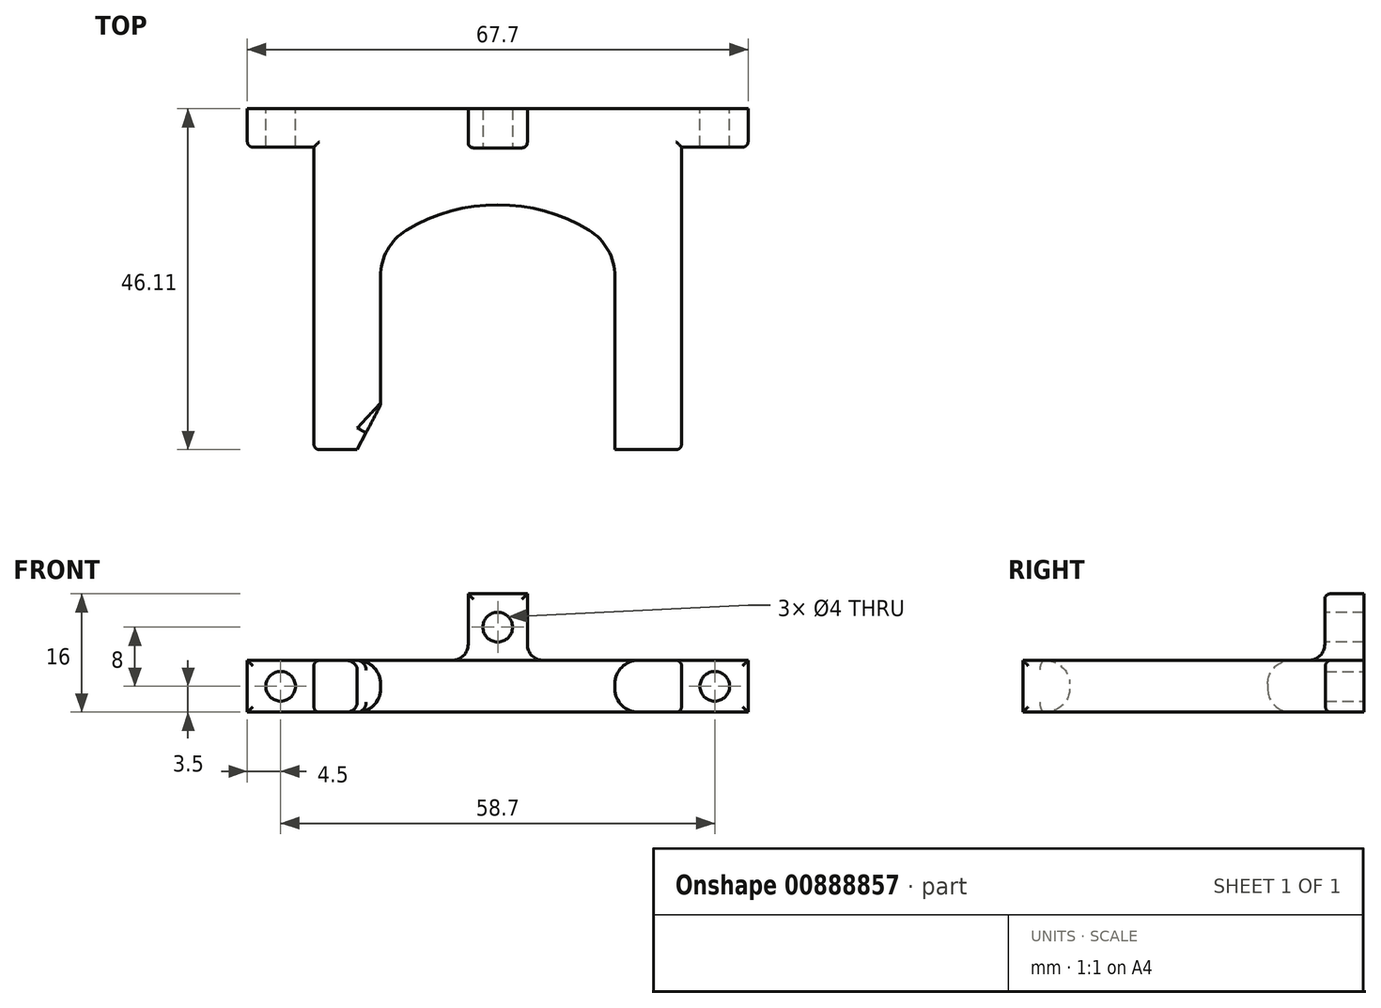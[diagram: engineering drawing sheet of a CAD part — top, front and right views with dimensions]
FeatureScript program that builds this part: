
annotation { "Feature Type Name" : "Feature", "Feature Type Description" : "" }
export const myFeature = defineFeature(function(context is Context, id is Id, definition is map)
    precondition{}
    {
        {
            var Q0;
            Q0=qCreatedBy(makeId("Top.planeOp"),FACE);
            var sketch = newSketch(context, id + "F0", { "sketchPlane" : qUnion([Q0])});
            skLineSegment(sketch, "E0", {"start": v(-15.85, 0) * mm, "end": v(-15.85, -27.08) * mm});
            skLineSegment(sketch, "E1", {"start": v(-15.85, -27.08) * mm, "end": v(-24.85, -27.08) * mm});
            skLineSegment(sketch, "E2", {"start": v(-24.85, -27.08) * mm, "end": v(-24.85, 19.03) * mm});
            skLineSegment(sketch, "E3", {"start": v(-24.85, 19.03) * mm, "end": v(24.85, 19.03) * mm});
            skLineSegment(sketch, "E4", {"start": v(24.85, 19.03) * mm, "end": v(24.85, -27.08) * mm});
            skLineSegment(sketch, "E5", {"start": v(24.85, -27.08) * mm, "end": v(15.85, -27.08) * mm});
            skLineSegment(sketch, "E6", {"start": v(15.85, -27.08) * mm, "end": v(15.85, 0) * mm});
            skPoint(sketch, "E7", {"position": v(0, 0) * mm});
            skPoint(sketch, "E8", {"position": v(0, 19.03) * mm});
            skArc(sketch, "E9", {"start": v(15.85, 0) * mm, "mid": v(0, 6.03) * mm, "end": v(-15.85, 0) * mm});
            skSolve(sketch);
        }
        {
            var Q0;
            Q0 = qSketchRegion(id + "F0", true);
            extrude(context, id + "F1", {"entities" : qUnion([Q0]), "depth" : 7 * mm, "offsetDistance" : 25 * mm});
        }
        {
            var Q0;
            Q0=makeQuery(id+"F1.opExtrude","SWEPT_EDGE",EDGE,{"disambiguationData":[OSD([sQuery(id+"F0.wireOp",EDGE,"E0"),sQuery(id+"F0.wireOp",EDGE,"E9")])]});
            var Q1;
            Q1=makeQuery(id+"F1.opExtrude","SWEPT_EDGE",EDGE,{"disambiguationData":[OSD([sQuery(id+"F0.wireOp",EDGE,"E6"),sQuery(id+"F0.wireOp",EDGE,"E9")])]});
            fillet(context, id + "F2", {"entities" : qUnion([Q0, Q1]), "radius" : 7.3 * mm, "tangentPropagation" : true, "allowEdgeOverflow" : false});
        }
        {
            var Q0;
            Q0=makeQuery(id+"F1.opExtrude","CAP_EDGE",EDGE,{"disambiguationData":[OSD([sQuery(id+"F0.wireOp",EDGE,"E0")])],"isStart":false});
            var Q1;
            {var subQ0=sQuery(id+"F0.wireOp",EDGE,"E9");var subQ1=sQuery(id+"F0.wireOp",EDGE,"E0");Q1=makeQuery(id+"F2.opFillet","BLEND_EDGE",EDGE,{"blendedFrom":[makeQuery(id+"F1.opExtrude","SWEPT_EDGE",EDGE,{"disambiguationData":[OSD([subQ1,subQ0])]}),makeQuery(id+"F1.opExtrude","CAP_FACE",FACE,{"disambiguationData":[OSD([subQ1,sQuery(id+"F0.wireOp",EDGE,"E1"),sQuery(id+"F0.wireOp",EDGE,"E2"),sQuery(id+"F0.wireOp",EDGE,"E3"),sQuery(id+"F0.wireOp",EDGE,"E4"),sQuery(id+"F0.wireOp",EDGE,"E5"),sQuery(id+"F0.wireOp",EDGE,"E6"),subQ0])],"isStart":false})],"blendedInto":[makeQuery(id+"F1.opExtrude","CAP_FACE",FACE,{"disambiguationData":[OSD([subQ1,sQuery(id+"F0.wireOp",EDGE,"E1"),sQuery(id+"F0.wireOp",EDGE,"E2"),sQuery(id+"F0.wireOp",EDGE,"E3"),sQuery(id+"F0.wireOp",EDGE,"E4"),sQuery(id+"F0.wireOp",EDGE,"E5"),sQuery(id+"F0.wireOp",EDGE,"E6"),subQ0])],"isStart":false})]});}
            var Q2;
            Q2=makeQuery(id+"F1.opExtrude","CAP_EDGE",EDGE,{"disambiguationData":[OSD([sQuery(id+"F0.wireOp",EDGE,"E9")])],"isStart":false});
            var Q3;
            {var subQ0=sQuery(id+"F0.wireOp",EDGE,"E9");var subQ1=sQuery(id+"F0.wireOp",EDGE,"E6");Q3=makeQuery(id+"F2.opFillet","BLEND_EDGE",EDGE,{"blendedFrom":[makeQuery(id+"F1.opExtrude","SWEPT_EDGE",EDGE,{"disambiguationData":[OSD([subQ1,subQ0])]}),makeQuery(id+"F1.opExtrude","CAP_FACE",FACE,{"disambiguationData":[OSD([sQuery(id+"F0.wireOp",EDGE,"E0"),sQuery(id+"F0.wireOp",EDGE,"E1"),sQuery(id+"F0.wireOp",EDGE,"E2"),sQuery(id+"F0.wireOp",EDGE,"E3"),sQuery(id+"F0.wireOp",EDGE,"E4"),sQuery(id+"F0.wireOp",EDGE,"E5"),subQ1,subQ0])],"isStart":false})],"blendedInto":[makeQuery(id+"F1.opExtrude","CAP_FACE",FACE,{"disambiguationData":[OSD([sQuery(id+"F0.wireOp",EDGE,"E0"),sQuery(id+"F0.wireOp",EDGE,"E1"),sQuery(id+"F0.wireOp",EDGE,"E2"),sQuery(id+"F0.wireOp",EDGE,"E3"),sQuery(id+"F0.wireOp",EDGE,"E4"),sQuery(id+"F0.wireOp",EDGE,"E5"),subQ1,subQ0])],"isStart":false})]});}
            var Q4;
            Q4=makeQuery(id+"F1.opExtrude","CAP_EDGE",EDGE,{"disambiguationData":[OSD([sQuery(id+"F0.wireOp",EDGE,"E6")])],"isStart":false});
            var Q5;
            Q5=makeQuery(id+"F1.opExtrude","CAP_EDGE",EDGE,{"disambiguationData":[OSD([sQuery(id+"F0.wireOp",EDGE,"E6")])],"isStart":true});
            var Q6;
            {var subQ0=sQuery(id+"F0.wireOp",EDGE,"E9");var subQ1=sQuery(id+"F0.wireOp",EDGE,"E6");Q6=makeQuery(id+"F2.opFillet","BLEND_EDGE",EDGE,{"blendedFrom":[makeQuery(id+"F1.opExtrude","SWEPT_EDGE",EDGE,{"disambiguationData":[OSD([subQ1,subQ0])]}),makeQuery(id+"F1.opExtrude","CAP_FACE",FACE,{"disambiguationData":[OSD([sQuery(id+"F0.wireOp",EDGE,"E0"),sQuery(id+"F0.wireOp",EDGE,"E1"),sQuery(id+"F0.wireOp",EDGE,"E2"),sQuery(id+"F0.wireOp",EDGE,"E3"),sQuery(id+"F0.wireOp",EDGE,"E4"),sQuery(id+"F0.wireOp",EDGE,"E5"),subQ1,subQ0])],"isStart":true})],"blendedInto":[makeQuery(id+"F1.opExtrude","CAP_FACE",FACE,{"disambiguationData":[OSD([sQuery(id+"F0.wireOp",EDGE,"E0"),sQuery(id+"F0.wireOp",EDGE,"E1"),sQuery(id+"F0.wireOp",EDGE,"E2"),sQuery(id+"F0.wireOp",EDGE,"E3"),sQuery(id+"F0.wireOp",EDGE,"E4"),sQuery(id+"F0.wireOp",EDGE,"E5"),subQ1,subQ0])],"isStart":true})]});}
            var Q7;
            Q7=makeQuery(id+"F1.opExtrude","CAP_EDGE",EDGE,{"disambiguationData":[OSD([sQuery(id+"F0.wireOp",EDGE,"E9")])],"isStart":true});
            var Q8;
            {var subQ0=sQuery(id+"F0.wireOp",EDGE,"E9");var subQ1=sQuery(id+"F0.wireOp",EDGE,"E0");Q8=makeQuery(id+"F2.opFillet","BLEND_EDGE",EDGE,{"blendedFrom":[makeQuery(id+"F1.opExtrude","SWEPT_EDGE",EDGE,{"disambiguationData":[OSD([subQ1,subQ0])]}),makeQuery(id+"F1.opExtrude","CAP_FACE",FACE,{"disambiguationData":[OSD([subQ1,sQuery(id+"F0.wireOp",EDGE,"E1"),sQuery(id+"F0.wireOp",EDGE,"E2"),sQuery(id+"F0.wireOp",EDGE,"E3"),sQuery(id+"F0.wireOp",EDGE,"E4"),sQuery(id+"F0.wireOp",EDGE,"E5"),sQuery(id+"F0.wireOp",EDGE,"E6"),subQ0])],"isStart":true})],"blendedInto":[makeQuery(id+"F1.opExtrude","CAP_FACE",FACE,{"disambiguationData":[OSD([subQ1,sQuery(id+"F0.wireOp",EDGE,"E1"),sQuery(id+"F0.wireOp",EDGE,"E2"),sQuery(id+"F0.wireOp",EDGE,"E3"),sQuery(id+"F0.wireOp",EDGE,"E4"),sQuery(id+"F0.wireOp",EDGE,"E5"),sQuery(id+"F0.wireOp",EDGE,"E6"),subQ0])],"isStart":true})]});}
            var Q9;
            Q9=makeQuery(id+"F1.opExtrude","CAP_EDGE",EDGE,{"disambiguationData":[OSD([sQuery(id+"F0.wireOp",EDGE,"E0")])],"isStart":true});
            fillet(context, id + "F3", {"entities" : qUnion([Q0, Q1, Q2, Q3, Q4, Q5, Q6, Q7, Q8, Q9]), "radius" : 3.14 * mm, "tangentPropagation" : true, "allowEdgeOverflow" : false});
        }
        {
            var Q0;
            Q0=makeQuery(id+"F1.opExtrude","SWEPT_FACE",FACE,{"disambiguationData":[OSD([sQuery(id+"F0.wireOp",EDGE,"E3")])]});
            var sketch = newSketch(context, id + "F4", { "sketchPlane" : qUnion([Q0])});
            skPoint(sketch, "E10", {"position": v(0, 7) * mm});
            skLineSegment(sketch, "E11.bottom", {"start": v(-4, 7) * mm, "end": v(4, 7) * mm});
            skLineSegment(sketch, "E11.top", {"start": v(-4, 16) * mm, "end": v(4, 16) * mm});
            skLineSegment(sketch, "E11.left", {"start": v(-4, 7) * mm, "end": v(-4, 16) * mm});
            skLineSegment(sketch, "E11.right", {"start": v(4, 7) * mm, "end": v(4, 16) * mm});
            skPoint(sketch, "E12", {"position": v(0, 16) * mm});
            skSolve(sketch);
        }
        {
            var Q0;
            Q0 = qSketchRegion(id + "F4", true);
            extrude(context, id + "F5", {"entities" : qUnion([Q0]), "operationType" : NewBodyOperationType.ADD, "oppositeDirection" : true, "depth" : 5.3 * mm, "offsetDistance" : 25 * mm});
        }
        {
            var Q0;
            Q0=makeQuery(id+"F5.opExtrude","CAP_FACE",FACE,{"disambiguationData":[OSD([sQuery(id+"F4.wireOp",EDGE,"E11.bottom"),sQuery(id+"F4.wireOp",EDGE,"E11.top"),sQuery(id+"F4.wireOp",EDGE,"E11.left"),sQuery(id+"F4.wireOp",EDGE,"E11.right")])],"isStart":false});
            var sketch = newSketch(context, id + "F6", { "sketchPlane" : qUnion([Q0])});
            skPoint(sketch, "E13", {"position": v(0, 11.5) * mm});
            skCircle(sketch, "E14", {"center": v(0, 11.5) * mm, "radius": 2 * mm});
            skSolve(sketch);
        }
        {
            var Q0;
            Q0 = qSketchRegion(id + "F6", true);
            extrude(context, id + "F7", {"entities" : qUnion([Q0]), "operationType" : NewBodyOperationType.REMOVE, "oppositeDirection" : true, "depth" : 25 * mm, "offsetDistance" : 25 * mm});
        }
        {
            var Q0;
            Q0=makeQuery(id+"F5.boolean.opBoolean","MERGE",FACE,{"derivedFrom":[makeQuery(id+"F1.opExtrude","SWEPT_FACE",FACE,{"disambiguationData":[OSD([sQuery(id+"F0.wireOp",EDGE,"E3")])]}),makeQuery(id+"F5.opExtrude","CAP_FACE",FACE,{"disambiguationData":[OSD([sQuery(id+"F4.wireOp",EDGE,"E11.bottom"),sQuery(id+"F4.wireOp",EDGE,"E11.top"),sQuery(id+"F4.wireOp",EDGE,"E11.left"),sQuery(id+"F4.wireOp",EDGE,"E11.right")])],"isStart":true})]});
            var sketch = newSketch(context, id + "F8", { "sketchPlane" : qUnion([Q0])});
            skLineSegment(sketch, "E15.bottom", {"start": v(24.85, 7) * mm, "end": v(33.85, 7) * mm});
            skLineSegment(sketch, "E15.top", {"start": v(24.85, 0) * mm, "end": v(33.85, 0) * mm});
            skLineSegment(sketch, "E15.left", {"start": v(24.85, 7) * mm, "end": v(24.85, 0) * mm});
            skLineSegment(sketch, "E15.right", {"start": v(33.85, 7) * mm, "end": v(33.85, 0) * mm});
            skLineSegment(sketch, "E16", {"start": v(0, 32.28) * mm, "end": v(0, -10.36) * mm});
            skPoint(sketch, "E16.endSnap0", {"position": v(0, 16) * mm});
            skLineSegment(sketch, "E17.MirrorCS", {"start": v(-24.85, 7) * mm, "end": v(-24.85, 0) * mm});
            skLineSegment(sketch, "E18.MirrorCS", {"start": v(-33.85, 7) * mm, "end": v(-33.85, 0) * mm});
            skLineSegment(sketch, "E19.MirrorCS", {"start": v(-24.85, 7) * mm, "end": v(-33.85, 7) * mm});
            skLineSegment(sketch, "E20.MirrorCS", {"start": v(-24.85, 0) * mm, "end": v(-33.85, 0) * mm});
            skSolve(sketch);
        }
        {
            var Q0;
            Q0 = qSketchRegion(id + "F8", true);
            extrude(context, id + "F9", {"entities" : qUnion([Q0]), "oppositeDirection" : true, "depth" : 5.2 * mm, "offsetDistance" : 25 * mm});
        }
        {
            var Q0;
            Q0=makeQuery(id+"F1.opExtrude","SWEPT_BODY",BODY,{"disambiguationData":[OSD([sQuery(id+"F0.wireOp",EDGE,"E0"),sQuery(id+"F0.wireOp",EDGE,"E1"),sQuery(id+"F0.wireOp",EDGE,"E2"),sQuery(id+"F0.wireOp",EDGE,"E3"),sQuery(id+"F0.wireOp",EDGE,"E4"),sQuery(id+"F0.wireOp",EDGE,"E5"),sQuery(id+"F0.wireOp",EDGE,"E6"),sQuery(id+"F0.wireOp",EDGE,"E9")])]});
            var Q1;
            Q1=makeQuery(id+"F9.opExtrude","SWEPT_BODY",BODY,{"disambiguationData":[OSD([sQuery(id+"F8.wireOp",EDGE,"E15.bottom"),sQuery(id+"F8.wireOp",EDGE,"E15.top"),sQuery(id+"F8.wireOp",EDGE,"E15.left"),sQuery(id+"F8.wireOp",EDGE,"E15.right")])]});
            var Q2;
            Q2=makeQuery(id+"F9.opExtrude","SWEPT_BODY",BODY,{"disambiguationData":[OSD([sQuery(id+"F8.wireOp",EDGE,"E17.MirrorCS"),sQuery(id+"F8.wireOp",EDGE,"E18.MirrorCS"),sQuery(id+"F8.wireOp",EDGE,"E19.MirrorCS"),sQuery(id+"F8.wireOp",EDGE,"E20.MirrorCS")])]});
            booleanBodies(context, id + "F10", {"operationType" : BooleanOperationType.UNION, "tools" : qUnion([Q0, Q1, Q2])});
        }
        {
            var Q0;
            Q0=makeQuery(id+"F10.opBoolean","MERGE",FACE,{"derivedFrom":[makeQuery(id+"F5.boolean.opBoolean","MERGE",FACE,{"derivedFrom":[makeQuery(id+"F1.opExtrude","SWEPT_FACE",FACE,{"disambiguationData":[OSD([sQuery(id+"F0.wireOp",EDGE,"E3")])]}),makeQuery(id+"F5.opExtrude","CAP_FACE",FACE,{"disambiguationData":[OSD([sQuery(id+"F4.wireOp",EDGE,"E11.bottom"),sQuery(id+"F4.wireOp",EDGE,"E11.top"),sQuery(id+"F4.wireOp",EDGE,"E11.left"),sQuery(id+"F4.wireOp",EDGE,"E11.right")])],"isStart":true})]}),makeQuery(id+"F9.opExtrude","CAP_FACE",FACE,{"disambiguationData":[OSD([sQuery(id+"F8.wireOp",EDGE,"E15.bottom"),sQuery(id+"F8.wireOp",EDGE,"E15.top"),sQuery(id+"F8.wireOp",EDGE,"E15.left"),sQuery(id+"F8.wireOp",EDGE,"E15.right")])],"isStart":true}),makeQuery(id+"F9.opExtrude","CAP_FACE",FACE,{"disambiguationData":[OSD([sQuery(id+"F8.wireOp",EDGE,"E17.MirrorCS"),sQuery(id+"F8.wireOp",EDGE,"E18.MirrorCS"),sQuery(id+"F8.wireOp",EDGE,"E19.MirrorCS"),sQuery(id+"F8.wireOp",EDGE,"E20.MirrorCS")])],"isStart":true})]});
            var sketch = newSketch(context, id + "F11", { "sketchPlane" : qUnion([Q0])});
            skLineSegment(sketch, "E21", {"start": v(0, 42.22) * mm, "end": v(0, -24.35) * mm});
            skCircle(sketch, "E22", {"center": v(29.35, 3.5) * mm, "radius": 2 * mm});
            skCircle(sketch, "E23.MirrorC", {"center": v(-29.35, 3.5) * mm, "radius": 2 * mm});
            skSolve(sketch);
        }
        {
            var Q0;
            Q0 = qSketchRegion(id + "F11", true);
            extrude(context, id + "F12", {"entities" : qUnion([Q0]), "operationType" : NewBodyOperationType.REMOVE, "oppositeDirection" : true, "depth" : 25 * mm, "offsetDistance" : 25 * mm});
        }
        {
            var Q0;
            Q0=makeQuery(id+"F9.opExtrude","CAP_EDGE",EDGE,{"disambiguationData":[OSD([sQuery(id+"F8.wireOp",EDGE,"E15.right")])],"isStart":false});
            var Q1;
            Q1=makeQuery(id+"F5.opExtrude","CAP_EDGE",EDGE,{"disambiguationData":[OSD([sQuery(id+"F4.wireOp",EDGE,"E11.right")])],"isStart":false});
            var Q2;
            Q2=makeQuery(id+"F5.opExtrude","CAP_EDGE",EDGE,{"disambiguationData":[OSD([sQuery(id+"F4.wireOp",EDGE,"E11.top")])],"isStart":false});
            var Q3;
            Q3=makeQuery(id+"F5.opExtrude","CAP_EDGE",EDGE,{"disambiguationData":[OSD([sQuery(id+"F4.wireOp",EDGE,"E11.left")])],"isStart":false});
            var Q4;
            Q4=makeQuery(id+"F9.opExtrude","CAP_EDGE",EDGE,{"disambiguationData":[OSD([sQuery(id+"F8.wireOp",EDGE,"E19.MirrorCS")])],"isStart":false});
            var Q5;
            Q5=makeQuery(id+"F9.opExtrude","CAP_EDGE",EDGE,{"disambiguationData":[OSD([sQuery(id+"F8.wireOp",EDGE,"E20.MirrorCS")])],"isStart":false});
            var Q6;
            Q6=makeQuery(id+"F9.opExtrude","CAP_EDGE",EDGE,{"disambiguationData":[OSD([sQuery(id+"F8.wireOp",EDGE,"E18.MirrorCS")])],"isStart":false});
            var Q7;
            Q7=makeQuery(id+"F1.opExtrude","CAP_EDGE",EDGE,{"disambiguationData":[OSD([sQuery(id+"F0.wireOp",EDGE,"E4")])],"isStart":true});
            var Q8;
            Q8=makeQuery(id+"F1.opExtrude","CAP_EDGE",EDGE,{"disambiguationData":[OSD([sQuery(id+"F0.wireOp",EDGE,"E4")])],"isStart":false});
            var Q9;
            Q9=makeQuery(id+"F9.opExtrude","CAP_EDGE",EDGE,{"disambiguationData":[OSD([sQuery(id+"F8.wireOp",EDGE,"E15.bottom")])],"isStart":false});
            var Q10;
            Q10=makeQuery(id+"F9.opExtrude","CAP_EDGE",EDGE,{"disambiguationData":[OSD([sQuery(id+"F8.wireOp",EDGE,"E15.top")])],"isStart":false});
            var Q11;
            Q11=makeQuery(id+"F1.opExtrude","CAP_EDGE",EDGE,{"disambiguationData":[OSD([sQuery(id+"F0.wireOp",EDGE,"E2")])],"isStart":false});
            var Q12;
            Q12=makeQuery(id+"F1.opExtrude","CAP_EDGE",EDGE,{"disambiguationData":[OSD([sQuery(id+"F0.wireOp",EDGE,"E2")])],"isStart":true});
            var Q13;
            Q13=makeQuery(id+"F1.opExtrude","SWEPT_EDGE",EDGE,{"disambiguationData":[OSD([sQuery(id+"F0.wireOp",EDGE,"E1"),sQuery(id+"F0.wireOp",EDGE,"E2")])]});
            var Q14;
            Q14=makeQuery(id+"F1.opExtrude","SWEPT_EDGE",EDGE,{"disambiguationData":[OSD([sQuery(id+"F0.wireOp",EDGE,"E4"),sQuery(id+"F0.wireOp",EDGE,"E5")])]});
            fillet(context, id + "F13", {"entities" : qUnion([Q0, Q1, Q2, Q3, Q4, Q5, Q6, Q7, Q8, Q9, Q10, Q11, Q12, Q13, Q14]), "radius" : 0.72 * mm, "tangentPropagation" : true, "allowEdgeOverflow" : false});
        }
        {
            var Q0;
            Q0=makeQuery(id+"F5.opExtrude","SWEPT_EDGE",EDGE,{"disambiguationData":[OSD([sQuery(id+"F0.wireOp",EDGE,"E3"),sQuery(id+"F4.wireOp",EDGE,"E11.bottom"),sQuery(id+"F4.wireOp",EDGE,"E11.right")])]});
            var Q1;
            Q1=makeQuery(id+"F5.opExtrude","CAP_EDGE",EDGE,{"disambiguationData":[OSD([sQuery(id+"F4.wireOp",EDGE,"E11.bottom")])],"isStart":false});
            var Q2;
            Q2=makeQuery(id+"F13.opFillet","BLEND_EDGE",EDGE,{"blendedFrom":[makeQuery(id+"F5.opExtrude","CAP_EDGE",EDGE,{"disambiguationData":[OSD([sQuery(id+"F4.wireOp",EDGE,"E11.right")])],"isStart":false}),makeQuery(id+"F10.opBoolean","MERGE",FACE,{"derivedFrom":[makeQuery(id+"F1.opExtrude","CAP_FACE",FACE,{"disambiguationData":[OSD([sQuery(id+"F0.wireOp",EDGE,"E0"),sQuery(id+"F0.wireOp",EDGE,"E1"),sQuery(id+"F0.wireOp",EDGE,"E2"),sQuery(id+"F0.wireOp",EDGE,"E3"),sQuery(id+"F0.wireOp",EDGE,"E4"),sQuery(id+"F0.wireOp",EDGE,"E5"),sQuery(id+"F0.wireOp",EDGE,"E6"),sQuery(id+"F0.wireOp",EDGE,"E9")])],"isStart":false}),makeQuery(id+"F9.opExtrude","SWEPT_FACE",FACE,{"disambiguationData":[OSD([sQuery(id+"F8.wireOp",EDGE,"E15.bottom")])]}),makeQuery(id+"F9.opExtrude","SWEPT_FACE",FACE,{"disambiguationData":[OSD([sQuery(id+"F8.wireOp",EDGE,"E19.MirrorCS")])]})]})],"blendedInto":[makeQuery(id+"F10.opBoolean","MERGE",FACE,{"derivedFrom":[makeQuery(id+"F1.opExtrude","CAP_FACE",FACE,{"disambiguationData":[OSD([sQuery(id+"F0.wireOp",EDGE,"E0"),sQuery(id+"F0.wireOp",EDGE,"E1"),sQuery(id+"F0.wireOp",EDGE,"E2"),sQuery(id+"F0.wireOp",EDGE,"E3"),sQuery(id+"F0.wireOp",EDGE,"E4"),sQuery(id+"F0.wireOp",EDGE,"E5"),sQuery(id+"F0.wireOp",EDGE,"E6"),sQuery(id+"F0.wireOp",EDGE,"E9")])],"isStart":false}),makeQuery(id+"F9.opExtrude","SWEPT_FACE",FACE,{"disambiguationData":[OSD([sQuery(id+"F8.wireOp",EDGE,"E15.bottom")])]}),makeQuery(id+"F9.opExtrude","SWEPT_FACE",FACE,{"disambiguationData":[OSD([sQuery(id+"F8.wireOp",EDGE,"E19.MirrorCS")])]})]})]});
            var Q3;
            Q3=makeQuery(id+"F13.opFillet","BLEND_EDGE",EDGE,{"blendedFrom":[makeQuery(id+"F5.opExtrude","CAP_EDGE",EDGE,{"disambiguationData":[OSD([sQuery(id+"F4.wireOp",EDGE,"E11.left")])],"isStart":false}),makeQuery(id+"F10.opBoolean","MERGE",FACE,{"derivedFrom":[makeQuery(id+"F1.opExtrude","CAP_FACE",FACE,{"disambiguationData":[OSD([sQuery(id+"F0.wireOp",EDGE,"E0"),sQuery(id+"F0.wireOp",EDGE,"E1"),sQuery(id+"F0.wireOp",EDGE,"E2"),sQuery(id+"F0.wireOp",EDGE,"E3"),sQuery(id+"F0.wireOp",EDGE,"E4"),sQuery(id+"F0.wireOp",EDGE,"E5"),sQuery(id+"F0.wireOp",EDGE,"E6"),sQuery(id+"F0.wireOp",EDGE,"E9")])],"isStart":false}),makeQuery(id+"F9.opExtrude","SWEPT_FACE",FACE,{"disambiguationData":[OSD([sQuery(id+"F8.wireOp",EDGE,"E15.bottom")])]}),makeQuery(id+"F9.opExtrude","SWEPT_FACE",FACE,{"disambiguationData":[OSD([sQuery(id+"F8.wireOp",EDGE,"E19.MirrorCS")])]})]})],"blendedInto":[makeQuery(id+"F10.opBoolean","MERGE",FACE,{"derivedFrom":[makeQuery(id+"F1.opExtrude","CAP_FACE",FACE,{"disambiguationData":[OSD([sQuery(id+"F0.wireOp",EDGE,"E0"),sQuery(id+"F0.wireOp",EDGE,"E1"),sQuery(id+"F0.wireOp",EDGE,"E2"),sQuery(id+"F0.wireOp",EDGE,"E3"),sQuery(id+"F0.wireOp",EDGE,"E4"),sQuery(id+"F0.wireOp",EDGE,"E5"),sQuery(id+"F0.wireOp",EDGE,"E6"),sQuery(id+"F0.wireOp",EDGE,"E9")])],"isStart":false}),makeQuery(id+"F9.opExtrude","SWEPT_FACE",FACE,{"disambiguationData":[OSD([sQuery(id+"F8.wireOp",EDGE,"E15.bottom")])]}),makeQuery(id+"F9.opExtrude","SWEPT_FACE",FACE,{"disambiguationData":[OSD([sQuery(id+"F8.wireOp",EDGE,"E19.MirrorCS")])]})]})]});
            var Q4;
            Q4=makeQuery(id+"F5.opExtrude","SWEPT_EDGE",EDGE,{"disambiguationData":[OSD([sQuery(id+"F0.wireOp",EDGE,"E3"),sQuery(id+"F4.wireOp",EDGE,"E11.bottom"),sQuery(id+"F4.wireOp",EDGE,"E11.left")])]});
            fillet(context, id + "F14", {"entities" : qUnion([Q0, Q1, Q2, Q3, Q4]), "radius" : 2.17 * mm, "tangentPropagation" : true, "allowEdgeOverflow" : false});
        }
        {
            var Q0;
            Q0=makeQuery(id+"F10.opBoolean","MERGE",FACE,{"derivedFrom":[makeQuery(id+"F1.opExtrude","CAP_FACE",FACE,{"disambiguationData":[OSD([sQuery(id+"F0.wireOp",EDGE,"E0"),sQuery(id+"F0.wireOp",EDGE,"E1"),sQuery(id+"F0.wireOp",EDGE,"E2"),sQuery(id+"F0.wireOp",EDGE,"E3"),sQuery(id+"F0.wireOp",EDGE,"E4"),sQuery(id+"F0.wireOp",EDGE,"E5"),sQuery(id+"F0.wireOp",EDGE,"E6"),sQuery(id+"F0.wireOp",EDGE,"E9")])],"isStart":false}),makeQuery(id+"F9.opExtrude","SWEPT_FACE",FACE,{"disambiguationData":[OSD([sQuery(id+"F8.wireOp",EDGE,"E15.bottom")])]}),makeQuery(id+"F9.opExtrude","SWEPT_FACE",FACE,{"disambiguationData":[OSD([sQuery(id+"F8.wireOp",EDGE,"E19.MirrorCS")])]})]});
            var sketch = newSketch(context, id + "F15", { "sketchPlane" : qUnion([Q0])});
            skLineSegment(sketch, "E24", {"start": v(-18.99, -27.08) * mm, "end": v(-11.63, -13.02) * mm});
            skLineSegment(sketch, "E25", {"start": v(12.4, -14.5) * mm, "end": v(18.99, -27.08) * mm});
            skLineSegment(sketch, "E26", {"start": v(18.99, -27.08) * mm, "end": v(-18.99, -27.08) * mm});
            skLineSegment(sketch, "E27", {"start": v(-11.63, -13.02) * mm, "end": v(-11.63, -27.08) * mm});
            skLineSegment(sketch, "E28", {"start": v(12.4, -14.5) * mm, "end": v(12.4, -27.08) * mm});
            skPoint(sketch, "E29.orphan", {"position": v(0, 9.17) * mm});
            skSolve(sketch);
        }
        {
            var Q0;
            Q0 = qSketchRegion(id + "F15", true);
            extrude(context, id + "F16", {"entities" : qUnion([Q0]), "operationType" : NewBodyOperationType.REMOVE, "oppositeDirection" : true, "depth" : 25 * mm, "offsetDistance" : 25 * mm});
        }
        {
            var Q0;
            {var subQ0=sQuery(id+"F0.wireOp",EDGE,"E6");Q0=makeQuery(id+"F16.boolean.opBoolean","INTERSECT",EDGE,{"derivedFrom":[makeQuery(id+"F3.opFillet","BLEND_FACE",FACE,{"disambiguationData":[OSD([subQ0]),TDD([makeQuery(id+"F1.opExtrude","CAP_EDGE",EDGE,{"disambiguationData":[OSD([subQ0])],"isStart":false})])]}),makeQuery(id+"F16.opExtrude","SWEPT_FACE",FACE,{"disambiguationData":[OSD([sQuery(id+"F15.wireOp",EDGE,"E25")])]})]});}
            var Q1;
            {var subQ0=sQuery(id+"F0.wireOp",EDGE,"E6");Q1=makeQuery(id+"F16.boolean.opBoolean","INTERSECT",EDGE,{"derivedFrom":[makeQuery(id+"F3.opFillet","BLEND_FACE",FACE,{"disambiguationData":[OSD([subQ0]),TDD([makeQuery(id+"F1.opExtrude","CAP_EDGE",EDGE,{"disambiguationData":[OSD([subQ0])],"isStart":true})])]}),makeQuery(id+"F16.opExtrude","SWEPT_FACE",FACE,{"disambiguationData":[OSD([sQuery(id+"F15.wireOp",EDGE,"E25")])]})]});}
            var Q2;
            {var subQ0=sQuery(id+"F0.wireOp",EDGE,"E0");Q2=makeQuery(id+"F16.boolean.opBoolean","INTERSECT",EDGE,{"derivedFrom":[makeQuery(id+"F3.opFillet","BLEND_FACE",FACE,{"disambiguationData":[OSD([subQ0]),TDD([makeQuery(id+"F1.opExtrude","CAP_EDGE",EDGE,{"disambiguationData":[OSD([subQ0])],"isStart":false})])]}),makeQuery(id+"F16.opExtrude","SWEPT_FACE",FACE,{"disambiguationData":[OSD([sQuery(id+"F15.wireOp",EDGE,"E24")])]})]});}
            var Q3;
            {var subQ0=sQuery(id+"F0.wireOp",EDGE,"E0");Q3=makeQuery(id+"F16.boolean.opBoolean","INTERSECT",EDGE,{"derivedFrom":[makeQuery(id+"F3.opFillet","BLEND_FACE",FACE,{"disambiguationData":[OSD([subQ0]),TDD([makeQuery(id+"F1.opExtrude","CAP_EDGE",EDGE,{"disambiguationData":[OSD([subQ0])],"isStart":true})])]}),makeQuery(id+"F16.opExtrude","SWEPT_FACE",FACE,{"disambiguationData":[OSD([sQuery(id+"F15.wireOp",EDGE,"E24")])]})]});}
            fillet(context, id + "F17", {"entities" : qUnion([Q0, Q1, Q2, Q3]), "radius" : 1.35 * mm, "tangentPropagation" : true, "allowEdgeOverflow" : false});
        }
    });
